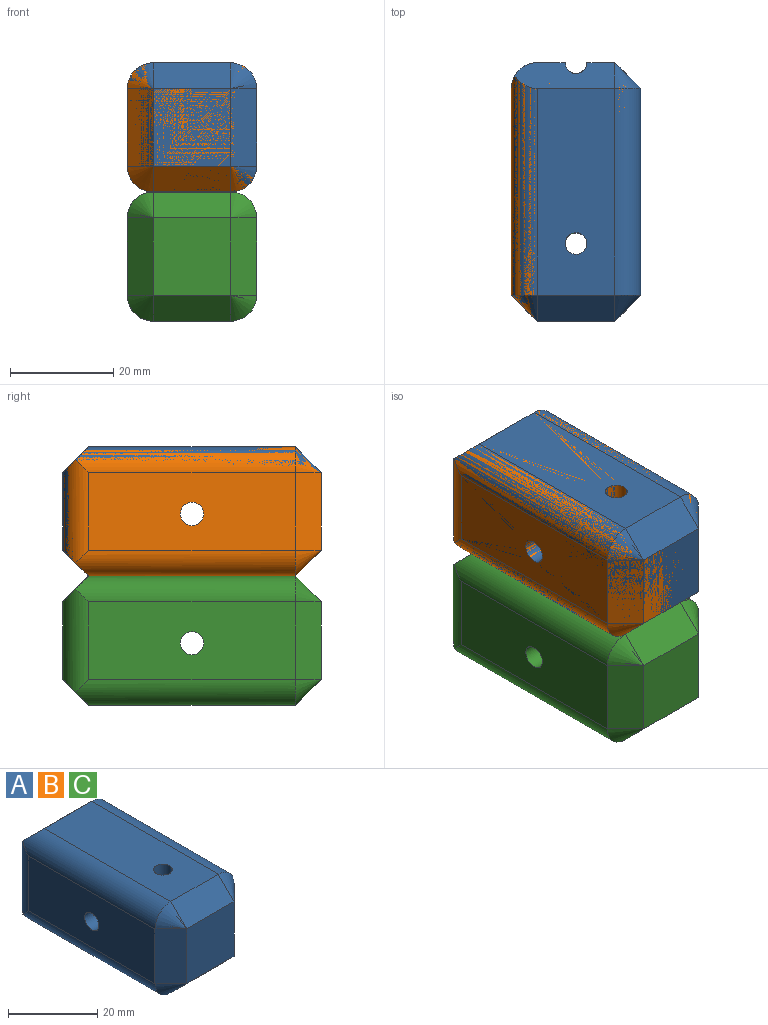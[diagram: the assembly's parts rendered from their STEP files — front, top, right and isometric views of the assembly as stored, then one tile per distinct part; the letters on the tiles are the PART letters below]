
ASSEMBLY  parts=3 mates=1
PART A: 30 faces, bbox 25x50x25 mm
  f0: plane 40x15mm, normal (0,0,1), area 586.1mm2, adj f11,f13,f14,f23,f28
  f1: plane 15x5.4mm, normal (0,1,0), area 81mm2, adj f22,f24,f28,f29
  f2: plane 15x5.4mm, normal (0,1,0), area 81mm2, adj f22,f24,f26,f28
  f3: plane 15x15mm, normal (0,-1,0), area 225mm2, adj f14,f17,f18,f21
  f4: plane 40x15mm, normal (0,0,-1), area 586.1mm2, adj f10,f12,f21,f23,f24
  f5: plane 40x15mm, normal (1,0,0), area 549.7mm2, adj f9,f12,f13,f17,f26
  f6: plane 40x15mm, normal (-1,0,0), area 584.1mm2, adj f7,f10,f11,f18,f29
  f7: cylinder r=2.25mm len=10mm, axis (1,0,0), area 141.4mm2, adj f6,f8
  f8: plane 8x8mm, normal (1,0,0), area 34.4mm2, adj f7,f9
  f9: cylinder r=4mm len=15mm, axis (1,0,0), area 377mm2, adj f5,f8
  f10: cylinder r=5mm len=42.5mm, axis (0,1,0), area 322mm2, adj f4,f6,f20,f24,f29
  f11: cylinder r=5mm len=42.5mm, axis (0,-1,0), area 322mm2, adj f0,f6,f16,f28,f29
  f12: cylinder r=5mm len=40mm, axis (0,-1,0), area 314.2mm2, adj f4,f5,f19,f25
  f13: cylinder r=5mm len=40mm, axis (0,1,0), area 314.2mm2, adj f0,f5,f15,f27
  f14: plane 15x5mm, normal (0,-0.71,0.71), area 106.1mm2, adj f0,f3,f15,f16
  f15: cone r=5mm half-angle=45deg, axis (0,1,0), area 27.8mm2, adj f13,f14,f17
  f16: cone r=5mm half-angle=45deg, axis (0,1,0), area 27.8mm2, adj f11,f14,f18
  f17: plane 15x5mm, normal (0.71,-0.71,0), area 106.1mm2, adj f3,f5,f15,f19
  f18: plane 15x5mm, normal (-0.71,-0.71,0), area 106.1mm2, adj f3,f6,f16,f20
  f19: cone r=5mm half-angle=45deg, axis (0,1,0), area 27.8mm2, adj f12,f17,f21
  f20: cone r=5mm half-angle=45deg, axis (0,1,0), area 27.8mm2, adj f10,f18,f21
  f21: plane 15x5mm, normal (0,-0.71,-0.71), area 106.1mm2, adj f3,f4,f19,f20
  f22: cylinder r=2.1mm len=19.21mm, axis (0,0,1), area 116.6mm2, adj f1,f2,f24,f28
  f23: cylinder r=2.1mm len=25mm, axis (0,0,1), area 329.9mm2, adj f0,f4
  f24: plane 19.33x5mm, normal (0,0.71,-0.71), area 118mm2, adj f1,f2,f4,f10,f22,f25,f29
  f25: cone r=5mm half-angle=45deg, axis (0,-1,0), area 27.8mm2, adj f12,f24,f26
  f26: plane 15x5mm, normal (0.71,0.71,0), area 106.1mm2, adj f2,f5,f25,f27
  f27: cone r=5mm half-angle=45deg, axis (0,-1,0), area 27.8mm2, adj f13,f26,f28
  f28: plane 19.33x5mm, normal (0,0.71,0.71), area 118mm2, adj f0,f1,f2,f11,f22,f27,f29
  f29: cylinder r=5mm len=20mm, axis (0,0,1), area 133.6mm2, adj f1,f6,f10,f11,f24,f28
PART B: same geometry as A
PART C: same geometry as A
PLACE A t=(-52.64,3.42,50.71)mm
PLACE B t=(-52.64,3.42,50.71)mm
PLACE C t=(-52.64,3.42,25.71)mm
MATE parallel C.f0 <-> B.f4  axis (0,0,1) through (-40.14,-21.35,50.71)mm
